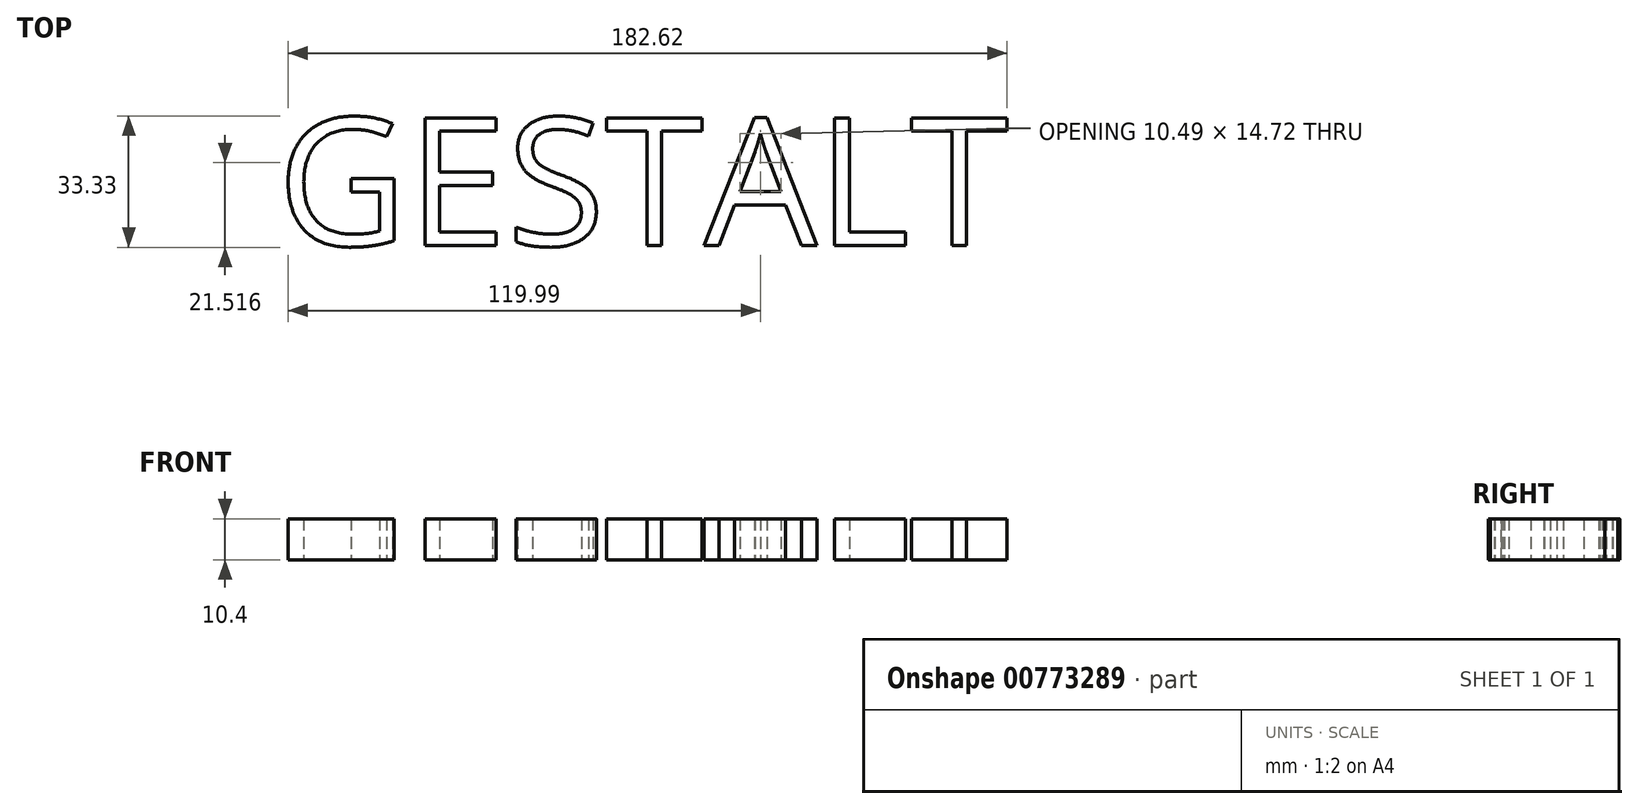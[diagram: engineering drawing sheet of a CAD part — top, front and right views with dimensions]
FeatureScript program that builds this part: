
annotation { "Feature Type Name" : "Feature", "Feature Type Description" : "" }
export const myFeature = defineFeature(function(context is Context, id is Id, definition is map)
    precondition{}
    {
        {
            var Q0;
            Q0=qCreatedBy(makeId("Top.planeOp"),FACE);
            var sketch = newSketch(context, id + "F0", { "sketchPlane" : qUnion([Q0])});
            skText(sketch, "E0", { "text": "GESTALT", "fontName": "OpenSans-Regular.ttf"});
            const initialGuessF0  = {"E0": [-0.04632, -0.05015, 1, 0, 0.0327]};
            skSetInitialGuess(sketch, initialGuessF0);
            skSolve(sketch);
        }
        {
            var Q0;
            Q0 = qSketchRegion(id + "F0", true);
            extrude(context, id + "F1", {"entities" : qUnion([Q0]), "depth" : 10.4 * mm, "offsetDistance" : 25 * mm});
        }
    });
